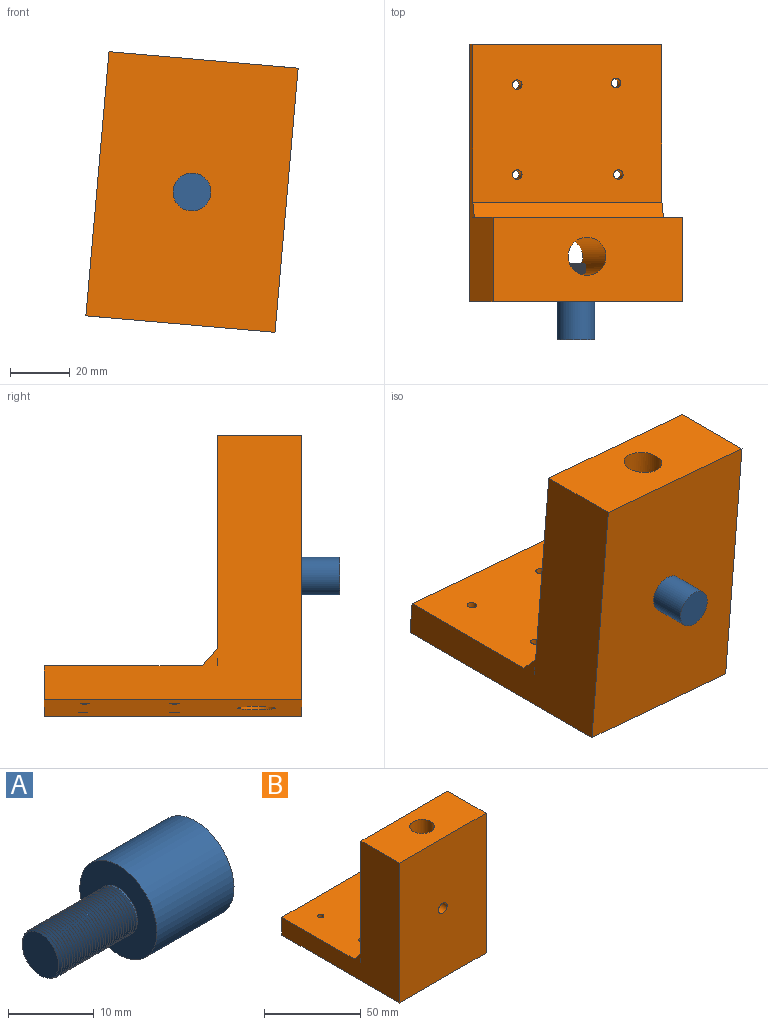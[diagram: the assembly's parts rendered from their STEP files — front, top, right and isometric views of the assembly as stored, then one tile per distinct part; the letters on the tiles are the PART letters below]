
ASSEMBLY  parts=2 mates=1
PART A: 10 faces, bbox 25.9x13x13 mm
  f0: plane 6.34x6.26mm, normal (-1,0,0), area 28.3mm2, adj f4,f5,f7,f8
  f1: cylinder r=6.35mm len=12.7mm, axis (-1,0,0), area 506.7mm2, adj f2,f3
  f2: plane 12.7x12.7mm, normal (1,0,0), area 126.7mm2, adj f1
  f3: plane 12.7x12.7mm, normal (-1,0,0), area 95mm2, adj f1,f4,f6
  f4: cylinder r=3.17mm len=12.7mm, axis (1,0,0), area 13.7mm2, adj f0,f3,f5,f7,f8,f9
  f5: plane 0.09x0.05mm, normal (0,0,1), area 0mm2, adj f0,f4,f8
  f6: cylinder r=3.17mm len=2.19mm, axis (1,0,0), area 0.1mm2, adj f3,f8,f9
  f7: bspline ~12.77x7.33mm, area 233mm2, adj f0,f4,f8,f9
  f8: bspline ~12.91x7.33mm, area 236.4mm2, adj f0,f4,f5,f6,f7,f9
  f9: plane 0.42x0.37mm, normal (0,0,-1), area 0.1mm2, adj f4,f6,f7,f8
PART B: 18 faces, bbox 63.5x86.1x88.7 mm
  f0: plane 63.5x0.02mm, normal (0,0,1), area 1.5mm2, adj f2,f8,f9,f16
  f1: plane 63.5x52.82mm, normal (0,0,1), area 3322.3mm2, adj f7,f8,f9,f12,f13,f14,f15,f17
  f2: plane 63.5x2.56mm, normal (0,1,0), area 162.3mm2, adj f0,f8,f9,f16
  f3: plane 71.54x63.5mm, normal (0,1,0), area 4542.8mm2, adj f4,f8,f9,f17
  f4: plane 63.5x28.16mm, normal (0,0,1), area 1661.6mm2, adj f3,f5,f8,f9,f10
  f5: plane 88.68x63.5mm, normal (0,-1,0), area 5599.6mm2, adj f4,f6,f8,f9,f11
  f6: plane 86.08x63.5mm, normal (0,0,-1), area 5308mm2, adj f5,f7,f8,f9,f10,f12,f13,f14
  f7: plane 63.5x11.38mm, normal (0,1,0), area 722.9mm2, adj f1,f6,f8,f9
  f8: plane 88.68x86.08mm, normal (1,0,0), area 3171.6mm2, adj f0,f1,f2,f3,f4,f5,f6,f7
  f9: plane 88.68x86.08mm, normal (-1,0,0), area 3171.6mm2, adj f0,f1,f2,f3,f4,f5,f6,f7
  f10: cylinder r=6.35mm len=88.68mm, axis (0,0,1), area 3505.4mm2, adj f4,f6,f11
  f11: cylinder r=3.17mm len=9.66mm, axis (0,-1,0), area 182mm2, adj f5,f10
  f12: cylinder r=1.59mm len=11.38mm, axis (0,0,1), area 113.6mm2, adj f1,f6
  f13: cylinder r=1.59mm len=11.38mm, axis (0,0,1), area 113.6mm2, adj f1,f6
  f14: cylinder r=1.59mm len=11.38mm, axis (0,0,1), area 113.6mm2, adj f1,f6
  f15: cylinder r=1.59mm len=11.38mm, axis (0,0,1), area 113.6mm2, adj f1,f6
  f16: plane 63.5x2.56mm, normal (0,-1,-0.01), area 162.3mm2, adj f0,f2,f8,f9
  f17: plane 63.5x5.76mm, normal (0,0.75,0.66), area 488.5mm2, adj f1,f3,f8,f9
PLACE A rot(axis=(0.71,-0.71,-0.03),176.5deg) t=(13.51,-73.56,15.45)mm
PLACE B rot(axis=(0,1,0),5deg) t=(-18.95,-61.21,8.73)mm
MATE parallel B.f11 <-> A.f1  axis (0,-1,0) through (13.51,-73.56,15.45)mm
